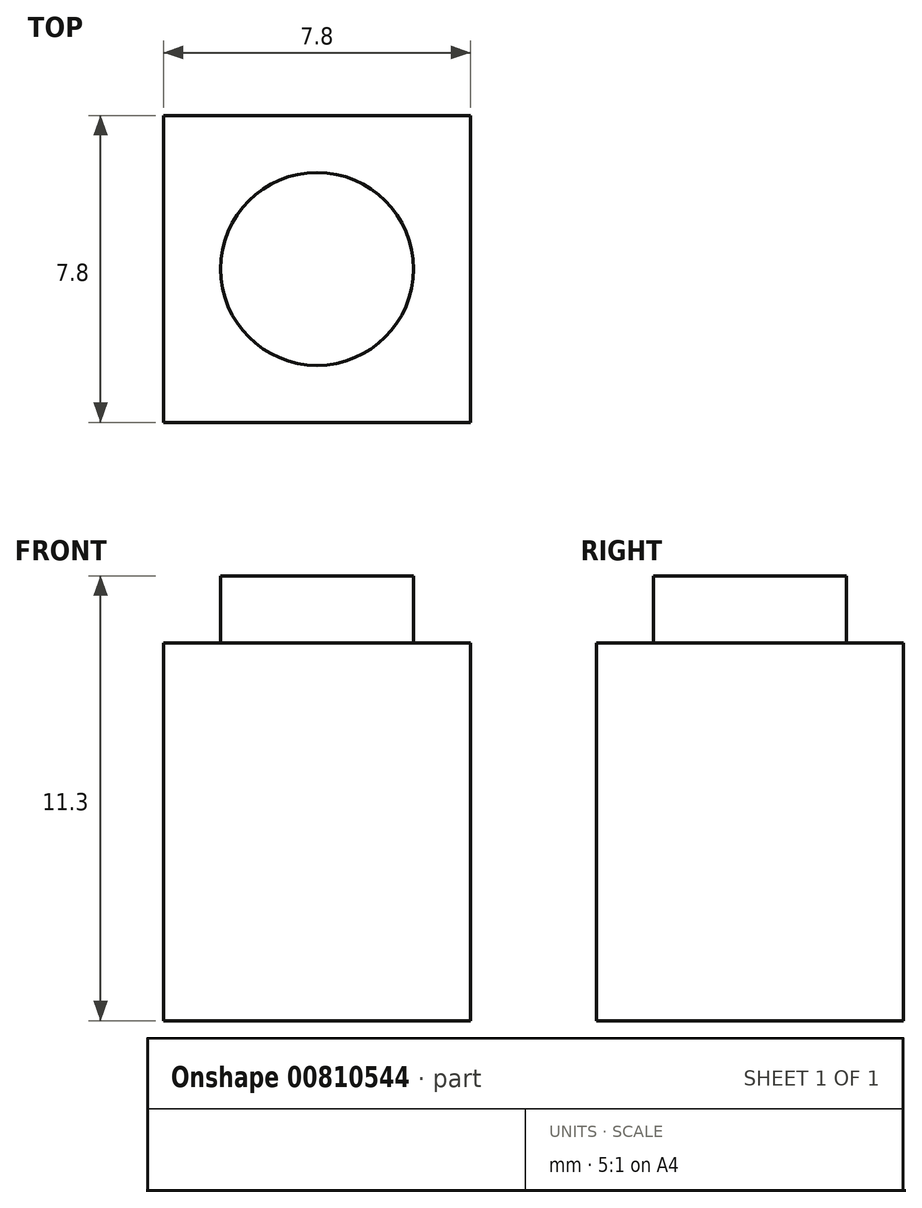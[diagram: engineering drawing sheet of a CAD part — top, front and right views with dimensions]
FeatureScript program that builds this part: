
annotation { "Feature Type Name" : "Feature", "Feature Type Description" : "" }
export const myFeature = defineFeature(function(context is Context, id is Id, definition is map)
    precondition{}
    {
        {
            var Q0;
            Q0=qCreatedBy(makeId("Top.planeOp"),FACE);
            var sketch = newSketch(context, id + "F0", { "sketchPlane" : qUnion([Q0])});
            skLineSegment(sketch, "E0", {"start": v(0, 0) * mm, "end": v(7.8, 0) * mm});
            skLineSegment(sketch, "E1", {"start": v(7.8, 0) * mm, "end": v(7.8, 7.8) * mm});
            skLineSegment(sketch, "E2", {"start": v(7.8, 7.8) * mm, "end": v(0, 7.8) * mm});
            skLineSegment(sketch, "E3", {"start": v(0, 7.8) * mm, "end": v(0, 0) * mm});
            skSolve(sketch);
        }
        {
            var Q0;
            Q0=makeQuery(id+"F0.imprint","IMPRINT",FACE,{"disambiguationData":[TD([[makeQuery(id+"F0.imprint","IMPRINT",EDGE,{"derivedFrom":sQuery(id+"F0.wireOp",EDGE,"E0")}),1.0]])]});
            extrude(context, id + "F1", {"entities" : qUnion([Q0]), "depth" : 9.6 * mm, "offsetDistance" : 25.4 * mm});
        }
        {
            var Q0;
            Q0=makeQuery(id+"F1.opExtrude","CAP_FACE",FACE,{"disambiguationData":[OSD([sQuery(id+"F0.wireOp",EDGE,"E0"),sQuery(id+"F0.wireOp",EDGE,"E1"),sQuery(id+"F0.wireOp",EDGE,"E2"),sQuery(id+"F0.wireOp",EDGE,"E3")])],"isStart":false});
            var sketch = newSketch(context, id + "F2", { "sketchPlane" : qUnion([Q0])});
            skLineSegment(sketch, "E4", {"start": v(0, 0) * mm, "end": v(3.9, 0) * mm, "construction": true});
            skLineSegment(sketch, "E5", {"start": v(3.9, 0) * mm, "end": v(3.9, 3.9) * mm, "construction": true});
            skPoint(sketch, "E5.endSnap0", {"position": v(3.9, 7.8) * mm});
            skCircle(sketch, "E6", {"center": v(3.9, 3.9) * mm, "radius": 2.45 * mm});
            skSolve(sketch);
        }
        {
            var Q0;
            Q0=makeQuery(id+"F2.imprint","IMPRINT",FACE,{"disambiguationData":[TD([[makeQuery(id+"F2.imprint","IMPRINT",EDGE,{"derivedFrom":sQuery(id+"F2.wireOp",EDGE,"E6")}),1.0]])]});
            extrude(context, id + "F3", {"entities" : qUnion([Q0]), "operationType" : NewBodyOperationType.ADD, "depth" : 1.7 * mm, "offsetDistance" : 25.4 * mm});
        }
    });
